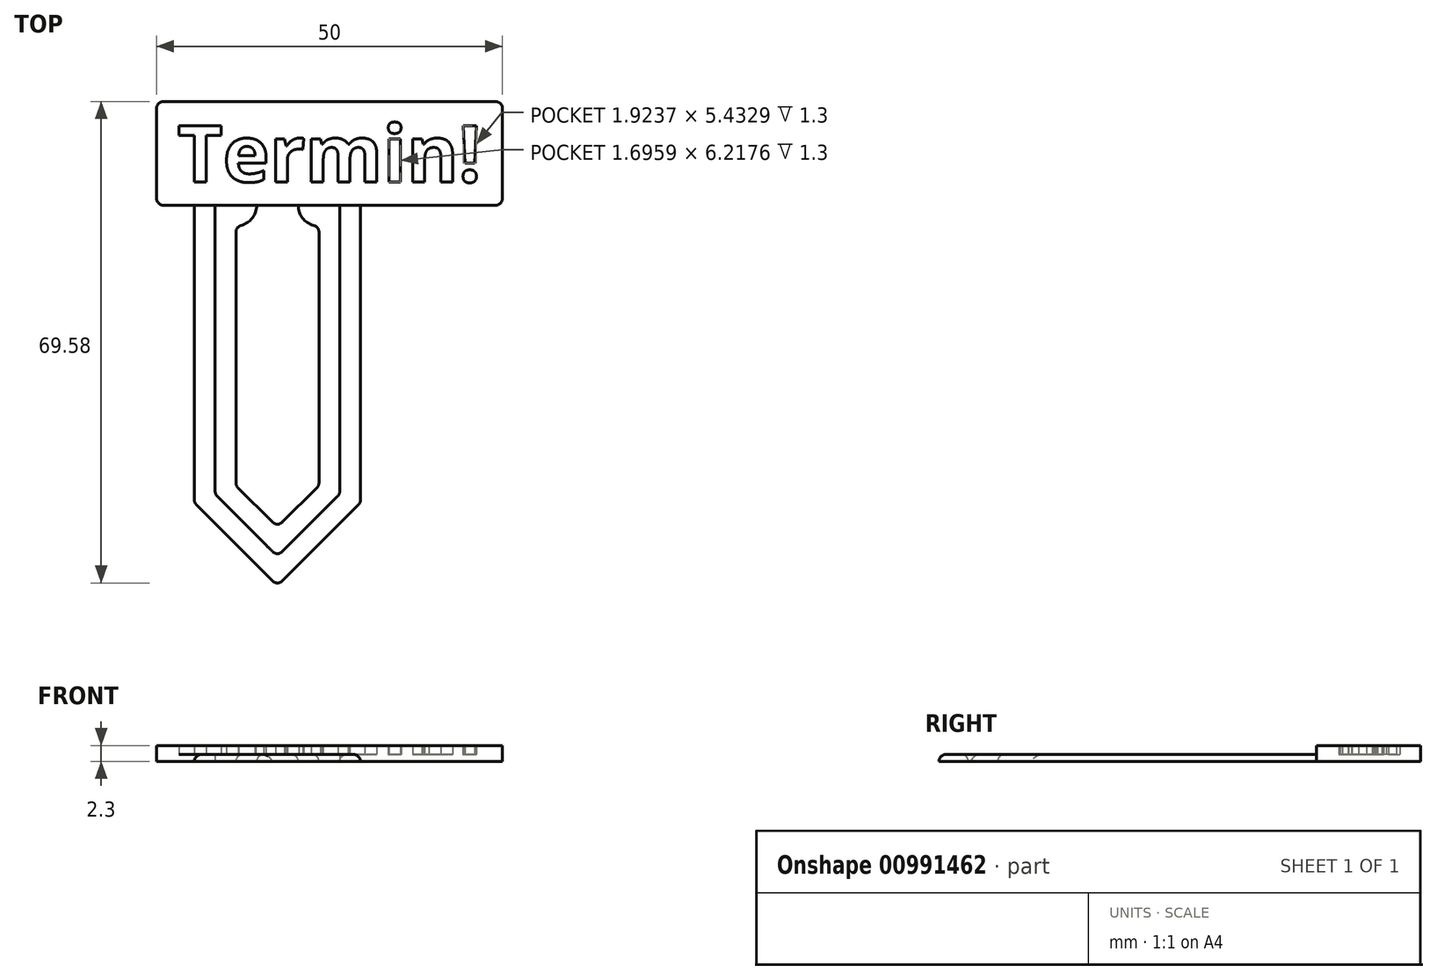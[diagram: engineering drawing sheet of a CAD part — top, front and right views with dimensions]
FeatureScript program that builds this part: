
annotation { "Feature Type Name" : "Feature", "Feature Type Description" : "" }
export const myFeature = defineFeature(function(context is Context, id is Id, definition is map)
    precondition{}
    {
        {
            var Q0;
            Q0=qCreatedBy(makeId("Top.planeOp"),FACE);
            var sketch = newSketch(context, id + "F0", { "sketchPlane" : qUnion([Q0])});
            skLineSegment(sketch, "E0", {"start": v(-14.18, 18.01) * mm, "end": v(-14.18, -24.99) * mm});
            skLineSegment(sketch, "E1", {"start": v(-11.18, 18.01) * mm, "end": v(-11.18, -23.75) * mm});
            skLineSegment(sketch, "E2", {"start": v(-8.18, 15.01) * mm, "end": v(-8.18, -22.5) * mm});
            skLineSegment(sketch, "E3", {"start": v(-2.18, 18.01) * mm, "end": v(-2.18, -9.23) * mm, "construction": true});
            skLineSegment(sketch, "E4", {"start": v(-8.18, -22.5) * mm, "end": v(-2.18, -28.5) * mm});
            skLineSegment(sketch, "E5", {"start": v(-11.18, -23.75) * mm, "end": v(-2.18, -32.75) * mm});
            skLineSegment(sketch, "E6", {"start": v(-2.18, -36.99) * mm, "end": v(-14.18, -24.99) * mm});
            skLineSegment(sketch, "E7.MirrorCS", {"start": v(9.82, 18.01) * mm, "end": v(9.82, -24.99) * mm});
            skLineSegment(sketch, "E8.MirrorCS", {"start": v(6.82, 18.01) * mm, "end": v(6.82, -23.75) * mm});
            skLineSegment(sketch, "E9.MirrorCS", {"start": v(3.82, -22.5) * mm, "end": v(-2.18, -28.5) * mm});
            skLineSegment(sketch, "E10.MirrorCS", {"start": v(6.82, -23.75) * mm, "end": v(-2.18, -32.75) * mm});
            skLineSegment(sketch, "E11.MirrorCS", {"start": v(3.82, 15.01) * mm, "end": v(3.82, -22.5) * mm});
            skLineSegment(sketch, "E12.MirrorCS", {"start": v(-2.18, -36.99) * mm, "end": v(9.82, -24.99) * mm});
            skLineSegment(sketch, "E13.bottom", {"start": v(30.35, 18.01) * mm, "end": v(-19.65, 18.01) * mm});
            skLineSegment(sketch, "E13.top", {"start": v(30.35, 33.01) * mm, "end": v(-19.65, 33.01) * mm});
            skLineSegment(sketch, "E13.left", {"start": v(30.35, 18.01) * mm, "end": v(30.35, 33.01) * mm});
            skLineSegment(sketch, "E13.right", {"start": v(-19.65, 18.01) * mm, "end": v(-19.65, 33.01) * mm});
            skArc(sketch, "E14", {"start": v(-5.18, 18.01) * mm, "mid": v(-6.06, 15.9) * mm, "end": v(-8.18, 15.01) * mm});
            skArc(sketch, "E15", {"start": v(0.82, 18.01) * mm, "mid": v(1.7, 15.9) * mm, "end": v(3.82, 15.01) * mm});
            skText(sketch, "E16", { "text": "Termin!", "fontName": "OpenSans-Bold.ttf"});
            skLineSegment(sketch, "E17", {"start": v(5.35, 33.01) * mm, "end": v(5.35, 18.01) * mm, "construction": true});
            skLineSegment(sketch, "E18", {"start": v(-19.65, 25.51) * mm, "end": v(30.35, 25.51) * mm, "construction": true});
            const initialGuessF0  = {"E16": [-0.01665, 0.0214, 1, 0, 0.0082]};
            skSetInitialGuess(sketch, initialGuessF0);
            skSolve(sketch);
        }
        {
            var Q0;
            {var subQ1=sQuery(id+"F0.wireOp",EDGE,"E0");Q0=makeQuery(id+"F0.imprint","IMPRINT",FACE,{"disambiguationData":[TD([[makeQuery(id+"F0.imprint","IMPRINT",EDGE,{"derivedFrom":subQ1}),1.0]])]});}
            var Q1;
            Q1=makeQuery(id+"F0.imprint","IMPRINT",FACE,{"disambiguationData":[TD([[makeQuery(id+"F0.imprint","IMPRINT",EDGE,{"derivedFrom":sQuery(id+"F0.wireOp",EDGE,"E2")}),1.0]])]});
            var Q2;
            Q2=makeQuery(id+"F0.imprint","IMPRINT",FACE,{"disambiguationData":[TD([[makeQuery(id+"F0.imprint","IMPRINT",EDGE,{"derivedFrom":sQuery(id+"F0.wireOp",EDGE,"E16.sketch_text.stroke-0")}),-1.0]])]});
            var Q3;
            Q3=makeQuery(id+"F0.imprint","IMPRINT",FACE,{"disambiguationData":[TD([[makeQuery(id+"F0.imprint","IMPRINT",EDGE,{"derivedFrom":sQuery(id+"F0.wireOp",EDGE,"E16.sketch_text.stroke-8")}),-1.0]])]});
            var Q4;
            Q4=makeQuery(id+"F0.imprint","IMPRINT",FACE,{"disambiguationData":[TD([[makeQuery(id+"F0.imprint","IMPRINT",EDGE,{"derivedFrom":sQuery(id+"F0.wireOp",EDGE,"E16.sketch_text.stroke-28")}),-1.0]])]});
            var Q5;
            Q5=makeQuery(id+"F0.imprint","IMPRINT",FACE,{"disambiguationData":[TD([[makeQuery(id+"F0.imprint","IMPRINT",EDGE,{"derivedFrom":sQuery(id+"F0.wireOp",EDGE,"E16.sketch_text.stroke-41")}),-1.0]])]});
            var Q6;
            Q6=makeQuery(id+"F0.imprint","IMPRINT",FACE,{"disambiguationData":[TD([[makeQuery(id+"F0.imprint","IMPRINT",EDGE,{"derivedFrom":sQuery(id+"F0.wireOp",EDGE,"E16.sketch_text.stroke-74")}),-1.0]])]});
            var Q7;
            Q7=makeQuery(id+"F0.imprint","IMPRINT",FACE,{"disambiguationData":[TD([[makeQuery(id+"F0.imprint","IMPRINT",EDGE,{"derivedFrom":sQuery(id+"F0.wireOp",EDGE,"E16.sketch_text.stroke-69")}),-1.0]])]});
            var Q8;
            Q8=makeQuery(id+"F0.imprint","IMPRINT",FACE,{"disambiguationData":[TD([[makeQuery(id+"F0.imprint","IMPRINT",EDGE,{"derivedFrom":sQuery(id+"F0.wireOp",EDGE,"E16.sketch_text.stroke-78")}),-1.0]])]});
            var Q9;
            Q9=makeQuery(id+"F0.imprint","IMPRINT",FACE,{"disambiguationData":[TD([[makeQuery(id+"F0.imprint","IMPRINT",EDGE,{"derivedFrom":sQuery(id+"F0.wireOp",EDGE,"E16.sketch_text.stroke-95")}),-1.0]])]});
            var Q10;
            Q10=makeQuery(id+"F0.imprint","IMPRINT",FACE,{"disambiguationData":[TD([[makeQuery(id+"F0.imprint","IMPRINT",EDGE,{"derivedFrom":sQuery(id+"F0.wireOp",EDGE,"E16.sketch_text.stroke-99")}),-1.0]])]});
            extrude(context, id + "F1", {"entities" : qUnion([Q0, Q1, Q2, Q3, Q4, Q5, Q6, Q7, Q8, Q9, Q10]), "depth" : 1 * mm, "offsetDistance" : 25 * mm});
        }
        {
            var Q0;
            Q0=makeQuery(id+"F0.imprint","IMPRINT",FACE,{"disambiguationData":[TD([[makeQuery(id+"F0.imprint","IMPRINT",EDGE,{"derivedFrom":sQuery(id+"F0.wireOp",EDGE,"E13.top")}),1.0]])]});
            var Q1;
            Q1=makeQuery(id+"F0.imprint","IMPRINT",FACE,{"disambiguationData":[TD([[makeQuery(id+"F0.imprint","IMPRINT",EDGE,{"derivedFrom":sQuery(id+"F0.wireOp",EDGE,"E16.sketch_text.stroke-8")}),1.0]])]});
            extrude(context, id + "F2", {"entities" : qUnion([Q0, Q1]), "operationType" : NewBodyOperationType.ADD, "depth" : 2.3 * mm, "offsetDistance" : 25 * mm});
        }
        {
            var Q0;
            Q0=makeQuery(id+"F2.opExtrude","SWEPT_EDGE",EDGE,{"disambiguationData":[OSD([sQuery(id+"F0.wireOp",EDGE,"E13.bottom"),sQuery(id+"F0.wireOp",EDGE,"E13.right")])]});
            var Q1;
            Q1=makeQuery(id+"F2.opExtrude","SWEPT_EDGE",EDGE,{"disambiguationData":[OSD([sQuery(id+"F0.wireOp",EDGE,"E13.top"),sQuery(id+"F0.wireOp",EDGE,"E13.right")])]});
            var Q2;
            Q2=makeQuery(id+"F2.opExtrude","SWEPT_EDGE",EDGE,{"disambiguationData":[OSD([sQuery(id+"F0.wireOp",EDGE,"E13.top"),sQuery(id+"F0.wireOp",EDGE,"E13.left")])]});
            var Q3;
            Q3=makeQuery(id+"F2.opExtrude","SWEPT_EDGE",EDGE,{"disambiguationData":[OSD([sQuery(id+"F0.wireOp",EDGE,"E13.bottom"),sQuery(id+"F0.wireOp",EDGE,"E13.left")])]});
            var Q4;
            Q4=makeQuery(id+"F1.opExtrude","SWEPT_EDGE",EDGE,{"disambiguationData":[OSD([sQuery(id+"F0.wireOp",EDGE,"E6"),sQuery(id+"F0.wireOp",EDGE,"E12.MirrorCS")])]});
            var Q5;
            Q5=makeQuery(id+"F1.opExtrude","SWEPT_EDGE",EDGE,{"disambiguationData":[OSD([sQuery(id+"F0.wireOp",EDGE,"E7.MirrorCS"),sQuery(id+"F0.wireOp",EDGE,"E12.MirrorCS")])]});
            var Q6;
            Q6=makeQuery(id+"F1.opExtrude","SWEPT_EDGE",EDGE,{"disambiguationData":[OSD([sQuery(id+"F0.wireOp",EDGE,"E0"),sQuery(id+"F0.wireOp",EDGE,"E6")])]});
            var Q7;
            Q7=makeQuery(id+"F1.opExtrude","SWEPT_EDGE",EDGE,{"disambiguationData":[OSD([sQuery(id+"F0.wireOp",EDGE,"E2"),sQuery(id+"F0.wireOp",EDGE,"E4")])]});
            var Q8;
            Q8=makeQuery(id+"F1.opExtrude","SWEPT_EDGE",EDGE,{"disambiguationData":[OSD([sQuery(id+"F0.wireOp",EDGE,"E4"),sQuery(id+"F0.wireOp",EDGE,"E9.MirrorCS")])]});
            var Q9;
            Q9=makeQuery(id+"F1.opExtrude","SWEPT_EDGE",EDGE,{"disambiguationData":[OSD([sQuery(id+"F0.wireOp",EDGE,"E9.MirrorCS"),sQuery(id+"F0.wireOp",EDGE,"E11.MirrorCS")])]});
            var Q10;
            Q10=makeQuery(id+"F1.opExtrude","SWEPT_EDGE",EDGE,{"disambiguationData":[OSD([sQuery(id+"F0.wireOp",EDGE,"E2"),sQuery(id+"F0.wireOp",EDGE,"E14")])]});
            var Q11;
            Q11=makeQuery(id+"F1.opExtrude","SWEPT_EDGE",EDGE,{"disambiguationData":[OSD([sQuery(id+"F0.wireOp",EDGE,"E11.MirrorCS"),sQuery(id+"F0.wireOp",EDGE,"E15")])]});
            var Q12;
            Q12=makeQuery(id+"F1.opExtrude","CAP_EDGE",EDGE,{"disambiguationData":[OSD([sQuery(id+"F0.wireOp",EDGE,"E12.MirrorCS")])],"isStart":false});
            var Q13;
            Q13=makeQuery(id+"F1.opExtrude","CAP_EDGE",EDGE,{"disambiguationData":[OSD([sQuery(id+"F0.wireOp",EDGE,"E7.MirrorCS")])],"isStart":false});
            var Q14;
            Q14=makeQuery(id+"F1.opExtrude","CAP_EDGE",EDGE,{"disambiguationData":[OSD([sQuery(id+"F0.wireOp",EDGE,"E6")])],"isStart":false});
            var Q15;
            Q15=makeQuery(id+"F1.opExtrude","CAP_EDGE",EDGE,{"disambiguationData":[OSD([sQuery(id+"F0.wireOp",EDGE,"E0")])],"isStart":false});
            var Q16;
            Q16=makeQuery(id+"F1.opExtrude","CAP_EDGE",EDGE,{"disambiguationData":[OSD([sQuery(id+"F0.wireOp",EDGE,"E11.MirrorCS")])],"isStart":false});
            var Q17;
            Q17=makeQuery(id+"F1.opExtrude","CAP_EDGE",EDGE,{"disambiguationData":[OSD([sQuery(id+"F0.wireOp",EDGE,"E15")])],"isStart":false});
            var Q18;
            Q18=makeQuery(id+"F1.opExtrude","CAP_EDGE",EDGE,{"disambiguationData":[OSD([sQuery(id+"F0.wireOp",EDGE,"E14")])],"isStart":false});
            var Q19;
            Q19=makeQuery(id+"F1.opExtrude","CAP_EDGE",EDGE,{"disambiguationData":[OSD([sQuery(id+"F0.wireOp",EDGE,"E2")])],"isStart":false});
            var Q20;
            Q20=makeQuery(id+"F1.opExtrude","CAP_EDGE",EDGE,{"disambiguationData":[OSD([sQuery(id+"F0.wireOp",EDGE,"E4")])],"isStart":false});
            var Q21;
            Q21=makeQuery(id+"F1.opExtrude","CAP_EDGE",EDGE,{"disambiguationData":[OSD([sQuery(id+"F0.wireOp",EDGE,"E9.MirrorCS")])],"isStart":false});
            var Q22;
            Q22=makeQuery(id+"F1.opExtrude","SWEPT_EDGE",EDGE,{"disambiguationData":[OSD([sQuery(id+"F0.wireOp",EDGE,"E1"),sQuery(id+"F0.wireOp",EDGE,"E5")])]});
            var Q23;
            Q23=makeQuery(id+"F1.opExtrude","SWEPT_EDGE",EDGE,{"disambiguationData":[OSD([sQuery(id+"F0.wireOp",EDGE,"E8.MirrorCS"),sQuery(id+"F0.wireOp",EDGE,"E10.MirrorCS")])]});
            var Q24;
            Q24=makeQuery(id+"F1.opExtrude","SWEPT_EDGE",EDGE,{"disambiguationData":[OSD([sQuery(id+"F0.wireOp",EDGE,"E5"),sQuery(id+"F0.wireOp",EDGE,"E10.MirrorCS")])]});
            var Q25;
            Q25=makeQuery(id+"F1.opExtrude","CAP_EDGE",EDGE,{"disambiguationData":[OSD([sQuery(id+"F0.wireOp",EDGE,"E10.MirrorCS")])],"isStart":false});
            fillet(context, id + "F3", {"entities" : qUnion([Q0, Q1, Q2, Q3, Q4, Q5, Q6, Q7, Q8, Q9, Q10, Q11, Q12, Q13, Q14, Q15, Q16, Q17, Q18, Q19, Q20, Q21, Q22, Q23, Q24, Q25]), "radius" : 1 * mm, "tangentPropagation" : true, "allowEdgeOverflow" : false});
        }
    });
